# Revit family: Keilhauer-Electric-Seater-
name_source: partatom
category: Furniture
units: mm (PartAtom-declared; Revit-internal decimal feet)

## family parameters
Always vertical = Yes
Cut with Voids When Loaded = No
OmniClass Number = 23.40.20.00
OmniClass Title = General Furniture and Specialties
Room Calculation Point = No
Shared = No
Work Plane-Based = No

## types (2) — shared parameters
Assembly Code = E2020200
Default Elevation = 0"
Keynote = 12500
Manufacturer = Keilhauer
Product Documentation Link = https://keilhauer.com
Revit File Built By = https://servex-us.com
Type Comments = Electric
URL = https://keilhauer.com

## per-type parameters (varying)
| type | Description | Dist Void Seat | Middle Seat | Width |
| 92000 | Two Seater Sofa | 31 3/4" | No | 63 1/2" |
| 92010 | Three Seater Sofa | 33 15/32" | Yes | 95" |

note: column(s) folded — value = type name in every type: Model

## geometry (parser evidence)
native form markers: Sweep x2
no freeform markers — native parametric forms only
